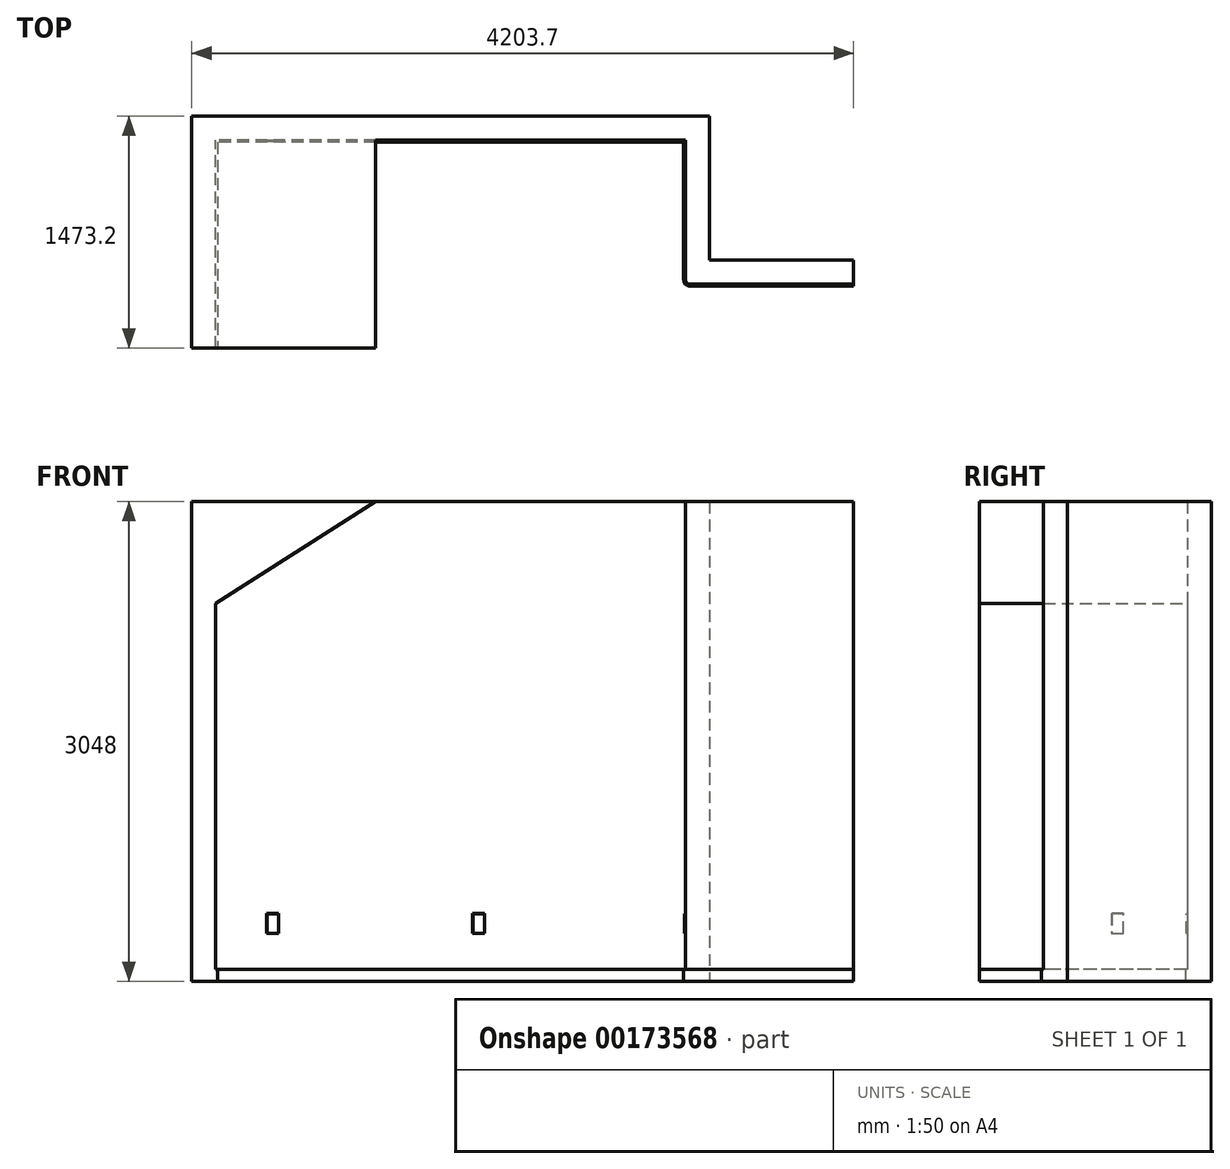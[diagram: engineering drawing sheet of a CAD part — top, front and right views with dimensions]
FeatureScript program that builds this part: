
annotation { "Feature Type Name" : "Feature", "Feature Type Description" : "" }
export const myFeature = defineFeature(function(context is Context, id is Id, definition is map)
    precondition{}
    {
        {
            var Q0;
            Q0=qCreatedBy(makeId("Top.planeOp"),FACE);
            var sketch = newSketch(context, id + "F0", { "sketchPlane" : qUnion([Q0])});
            skLineSegment(sketch, "E0.bottom", {"start": v(1492.25, 444.5) * mm, "end": v(-1492.25, 444.5) * mm});
            skLineSegment(sketch, "E0.top", {"start": v(1492.25, -444.5) * mm, "end": v(-1492.25, -444.5) * mm, "construction": true});
            skLineSegment(sketch, "E0.left", {"start": v(1492.25, 444.5) * mm, "end": v(1492.25, -444.5) * mm});
            skLineSegment(sketch, "E0.right", {"start": v(-1492.25, 444.5) * mm, "end": v(-1492.25, -444.5) * mm});
            skPoint(sketch, "E0.middle", {"position": v(0, 0) * mm});
            skArc(sketch, "E1", {"start": v(1517.65, -469.9) * mm, "mid": v(1499.69, -462.46) * mm, "end": v(1492.25, -444.5) * mm});
            skLineSegment(sketch, "E2", {"start": v(-1492.25, -444.5) * mm, "end": v(-1492.25, -876.3) * mm});
            skLineSegment(sketch, "E3", {"start": v(1517.65, -469.9) * mm, "end": v(2559.05, -469.9) * mm});
            skLineSegment(sketch, "E4.1", {"start": v(1644.65, -317.5) * mm, "end": v(2559.05, -317.5) * mm});
            skLineSegment(sketch, "E4.2", {"start": v(1644.65, 596.9) * mm, "end": v(1644.65, -317.5) * mm});
            skLineSegment(sketch, "E4.3", {"start": v(1644.65, 596.9) * mm, "end": v(-1644.65, 596.9) * mm});
            skLineSegment(sketch, "E4.4", {"start": v(-1644.65, 596.9) * mm, "end": v(-1644.65, -876.3) * mm});
            skLineSegment(sketch, "E5", {"start": v(-1492.25, -876.3) * mm, "end": v(-1644.65, -876.3) * mm});
            skLineSegment(sketch, "E6", {"start": v(2559.05, -317.5) * mm, "end": v(2559.05, -469.9) * mm});
            skLineSegment(sketch, "E7.0", {"start": v(1479.55, 431.8) * mm, "end": v(1479.55, -444.5) * mm});
            skLineSegment(sketch, "E7.4", {"start": v(-1479.55, 431.8) * mm, "end": v(-1479.55, -876.3) * mm});
            skLineSegment(sketch, "E7.6", {"start": v(1479.55, 431.8) * mm, "end": v(-1479.55, 431.8) * mm});
            skLineSegment(sketch, "E7.10", {"start": v(1517.65, -482.6) * mm, "end": v(2559.05, -482.6) * mm});
            skArc(sketch, "E7.11", {"start": v(1517.65, -482.6) * mm, "mid": v(1490.7, -471.44) * mm, "end": v(1479.55, -444.5) * mm});
            skLineSegment(sketch, "E8", {"start": v(2559.05, -469.9) * mm, "end": v(2559.05, -482.6) * mm});
            skLineSegment(sketch, "E9", {"start": v(-1492.25, -876.3) * mm, "end": v(-1479.55, -876.3) * mm});
            skSolve(sketch);
        }
        {
            var Q0;
            Q0=makeQuery(id+"F0.imprint","IMPRINT",FACE,{"disambiguationData":[TD([[makeQuery(id+"F0.imprint","IMPRINT",EDGE,{"derivedFrom":sQuery(id+"F0.wireOp",EDGE,"E0.bottom")}),-1.0]])]});
            extrude(context, id + "F1", {"entities" : qUnion([Q0]), "depth" : 3048 * mm});
        }
        {
            var Q0;
            Q0=makeQuery(id+"F0.imprint","IMPRINT",FACE,{"disambiguationData":[TD([[makeQuery(id+"F0.imprint","IMPRINT",EDGE,{"derivedFrom":sQuery(id+"F0.wireOp",EDGE,"E0.bottom")}),1.0]])]});
            extrude(context, id + "F2", {"entities" : qUnion([Q0]), "operationType" : NewBodyOperationType.ADD, "depth" : 76.2 * mm});
        }
        {
            var Q0;
            Q0=makeQuery(id+"F1.opExtrude","SWEPT_FACE",FACE,{"disambiguationData":[OSD([sQuery(id+"F0.wireOp",EDGE,"E0.bottom")])]});
            var sketch = newSketch(context, id + "F3", { "sketchPlane" : qUnion([Q0])});
            skLineSegment(sketch, "E10.bottom", {"start": v(-1168.4, 431.8) * mm, "end": v(-1092.2, 431.8) * mm});
            skLineSegment(sketch, "E10.top", {"start": v(-1168.4, 304.8) * mm, "end": v(-1092.2, 304.8) * mm});
            skLineSegment(sketch, "E10.left", {"start": v(-1168.4, 431.8) * mm, "end": v(-1168.4, 304.8) * mm});
            skLineSegment(sketch, "E10.right", {"start": v(-1092.2, 431.8) * mm, "end": v(-1092.2, 304.8) * mm});
            skLineSegment(sketch, "E11.bottom", {"start": v(139.7, 431.8) * mm, "end": v(215.9, 431.8) * mm});
            skLineSegment(sketch, "E11.top", {"start": v(139.7, 304.8) * mm, "end": v(215.9, 304.8) * mm});
            skLineSegment(sketch, "E11.left", {"start": v(139.7, 431.8) * mm, "end": v(139.7, 304.8) * mm});
            skLineSegment(sketch, "E11.right", {"start": v(215.9, 431.8) * mm, "end": v(215.9, 304.8) * mm});
            skLineSegment(sketch, "E12", {"start": v(-1492.25, 304.8) * mm, "end": v(1492.25, 304.8) * mm, "construction": true});
            skSolve(sketch);
        }
        {
            var Q0;
            Q0=makeQuery(id+"F3.imprint","IMPRINT",FACE,{"disambiguationData":[TD([[makeQuery(id+"F3.imprint","IMPRINT",EDGE,{"derivedFrom":sQuery(id+"F3.wireOp",EDGE,"E10.bottom")}),-1.0]])]});
            var Q1;
            Q1=makeQuery(id+"F3.imprint","IMPRINT",FACE,{"disambiguationData":[TD([[makeQuery(id+"F3.imprint","IMPRINT",EDGE,{"derivedFrom":sQuery(id+"F3.wireOp",EDGE,"E11.bottom")}),-1.0]])]});
            extrude(context, id + "F4", {"entities" : qUnion([Q0, Q1]), "operationType" : NewBodyOperationType.ADD, "depth" : 6.35 * mm, "hasDraft" : true, "draftAngle" : 15 * degree, "draftPullDirection" : true});
        }
        {
            var Q0;
            Q0=makeQuery(id+"F1.opExtrude","SWEPT_FACE",FACE,{"disambiguationData":[OSD([sQuery(id+"F0.wireOp",EDGE,"E0.left")])]});
            var sketch = newSketch(context, id + "F5", { "sketchPlane" : qUnion([Q0])});
            skLineSegment(sketch, "E13", {"start": v(-444.5, 304.8) * mm, "end": v(444.5, 304.8) * mm, "construction": true});
            skLineSegment(sketch, "E14.bottom", {"start": v(-38.1, 431.8) * mm, "end": v(38.1, 431.8) * mm});
            skLineSegment(sketch, "E14.top", {"start": v(-38.1, 304.8) * mm, "end": v(38.1, 304.8) * mm});
            skLineSegment(sketch, "E14.left", {"start": v(-38.1, 431.8) * mm, "end": v(-38.1, 304.8) * mm});
            skLineSegment(sketch, "E14.right", {"start": v(38.1, 431.8) * mm, "end": v(38.1, 304.8) * mm});
            skSolve(sketch);
        }
        {
            var Q0;
            Q0 = qSketchRegion(id + "F5", true);
            extrude(context, id + "F6", {"entities" : qUnion([Q0]), "operationType" : NewBodyOperationType.ADD, "depth" : 6.35 * mm, "hasDraft" : true, "draftAngle" : 15 * degree, "draftPullDirection" : true});
        }
        {
            var Q0;
            Q0=makeQuery(id+"F1.opExtrude","SWEPT_FACE",FACE,{"disambiguationData":[OSD([sQuery(id+"F0.wireOp",EDGE,"E0.bottom")])]});
            var sketch = newSketch(context, id + "F7", { "sketchPlane" : qUnion([Q0])});
            skLineSegment(sketch, "E15", {"start": v(-1492.25, 3048) * mm, "end": v(-476.25, 3048) * mm});
            skLineSegment(sketch, "E16", {"start": v(-476.25, 3048) * mm, "end": v(-1492.25, 2400.3) * mm});
            skSolve(sketch);
        }
        {
            var Q0;
            {var subQ0=sQuery(id+"F7.wireOp",EDGE,"E15");Q0=makeQuery(id+"F7.imprint","IMPRINT",FACE,{"disambiguationData":[TD([[makeQuery(id+"F7.imprint","IMPRINT",EDGE,{"derivedFrom":subQ0}),1.0]])]});}
            var Q1;
            Q1=makeQuery(id+"F2.boolean.opBoolean","MERGE",FACE,{"derivedFrom":[makeQuery(id+"F1.opExtrude","SWEPT_FACE",FACE,{"disambiguationData":[OSD([sQuery(id+"F0.wireOp",EDGE,"E5")])]}),makeQuery(id+"F2.opExtrude","SWEPT_FACE",FACE,{"disambiguationData":[OSD([sQuery(id+"F0.wireOp",EDGE,"E9")])]})]});
            extrude(context, id + "F8", {"entities" : qUnion([Q0]), "operationType" : NewBodyOperationType.ADD, "endBound" : BoundingType.UP_TO_SURFACE, "endBoundEntityFace" : qUnion([Q1]), "depth" : 25.4 * mm});
        }
    });
